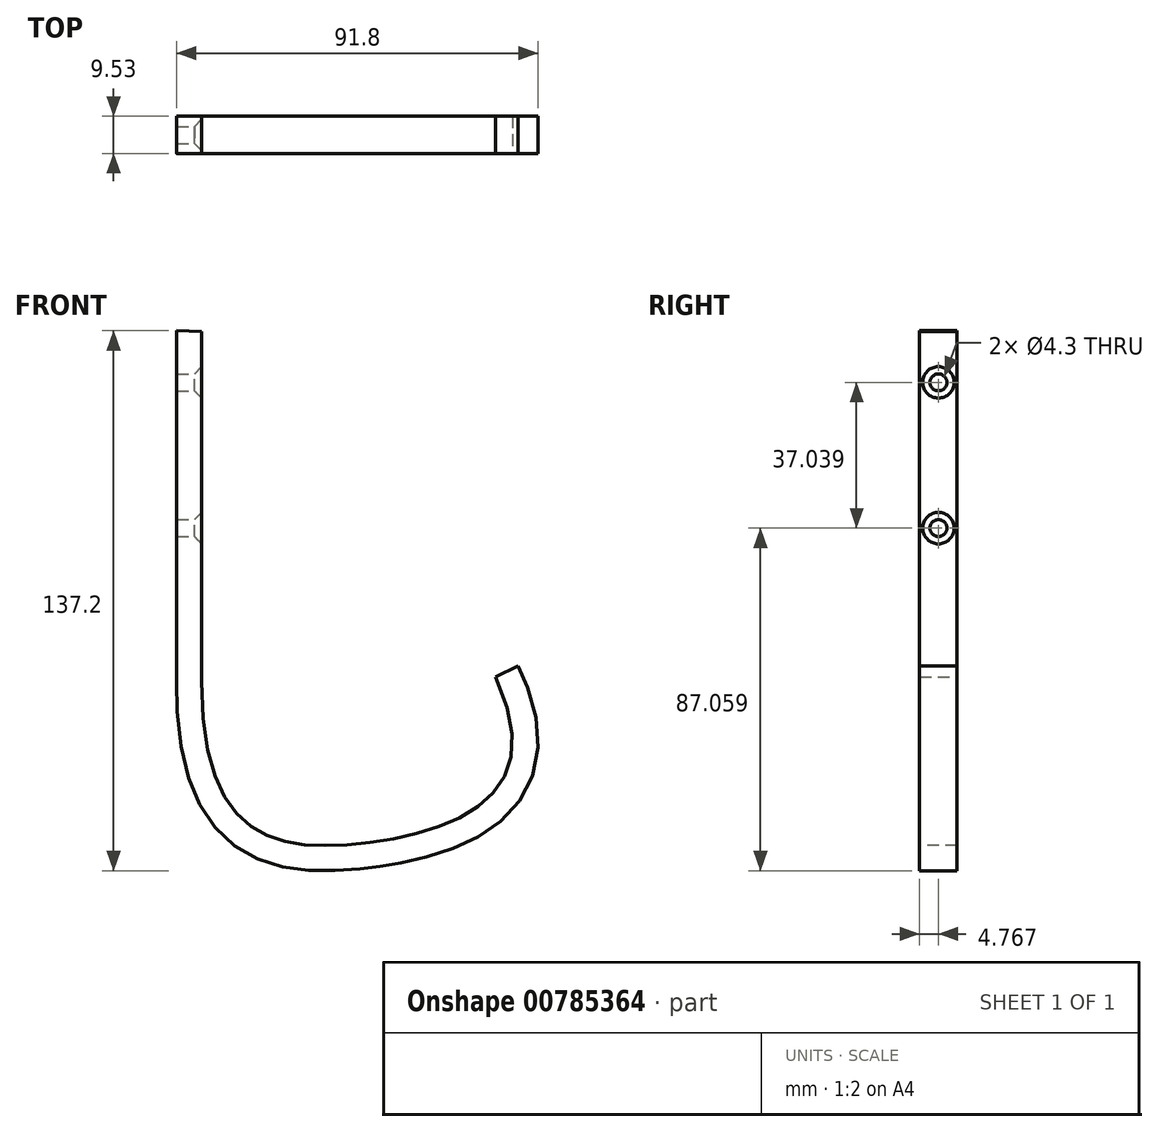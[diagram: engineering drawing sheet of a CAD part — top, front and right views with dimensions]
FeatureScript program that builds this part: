
annotation { "Feature Type Name" : "Feature", "Feature Type Description" : "" }
export const myFeature = defineFeature(function(context is Context, id is Id, definition is map)
    precondition{}
    {
        {
            var Q0;
            Q0=qCreatedBy(makeId("Front.planeOp"),FACE);
            var sketch = newSketch(context, id + "F0", { "sketchPlane" : qUnion([Q0])});
            skLineSegment(sketch, "E0", {"start": v(-38.57, 47.63) * mm, "end": v(-38.57, -41.27) * mm});
            skFitSpline(sketch, "E1", {"points": [v(-38.57, -41.27) * mm, v(2.43, -82.32) * mm, v(36.03, -40.1) * mm], "startDerivative": vector(0, -233.55) * mm, "endDerivative": vector(-90.62, 189.33) * mm});
            skFitSpline(sketch, "E2.0", {"points": [v(-44.92, -41.27) * mm, v(-44.92, -46.38) * mm, v(-44.5, -53.3) * mm, v(-43.08, -61.23) * mm, v(-41.58, -66.6) * mm, v(-39.63, -71.39) * mm, v(-37.22, -75.64) * mm, v(-34.35, -79.32) * mm, v(-31.05, -82.4) * mm, v(-27.41, -84.86) * mm, v(-23.53, -86.7) * mm, v(-19.49, -88) * mm, v(-15.34, -88.82) * mm, v(-11.12, -89.24) * mm, v(-6.84, -89.34) * mm, v(-2.51, -89.17) * mm, v(1.14, -88.85) * mm, v(4.08, -88.52) * mm, v(6.32, -88.23) * mm, v(8.58, -87.9) * mm, v(11.61, -87.38) * mm, v(15.43, -86.6) * mm, v(19.98, -85.42) * mm, v(24.44, -83.95) * mm, v(28.76, -82.14) * mm, v(32.88, -79.93) * mm, v(36.7, -77.24) * mm, v(40.15, -74.01) * mm, v(43.06, -70.17) * mm, v(45.24, -65.71) * mm, v(46.53, -60.73) * mm, v(46.84, -55.36) * mm, v(46.17, -49.7) * mm, v(44.54, -43.72) * mm, v(42.8, -39.52) * mm, v(41.76, -37.35) * mm]});
            skLineSegment(sketch, "E2.1", {"start": v(-44.92, 47.86) * mm, "end": v(-44.92, -41.27) * mm});
            skLineSegment(sketch, "E3", {"start": v(-44.92, 47.86) * mm, "end": v(-38.57, 47.63) * mm});
            skLineSegment(sketch, "E4", {"start": v(36.03, -40.1) * mm, "end": v(41.76, -37.35) * mm});
            skSolve(sketch);
        }
        {
            var Q0;
            Q0=makeQuery(id+"F0.imprint","IMPRINT",FACE,{"disambiguationData":[TD([[makeQuery(id+"F0.imprint","IMPRINT",EDGE,{"derivedFrom":sQuery(id+"F0.wireOp",EDGE,"E0")}),-1.0]])]});
            extrude(context, id + "F1", {"entities" : qUnion([Q0]), "depth" : 9.52 * mm, "offsetDistance" : 25.4 * mm});
        }
        {
            var Q0;
            Q0=makeQuery(id+"F1.opExtrude","SWEPT_FACE",FACE,{"disambiguationData":[OSD([sQuery(id+"F0.wireOp",EDGE,"E0")])]});
            var sketch = newSketch(context, id + "F2", { "sketchPlane" : qUnion([Q0])});
            skPoint(sketch, "E5", {"position": v(-4.76, 34.76) * mm});
            skPoint(sketch, "E6", {"position": v(-4.76, -2.28) * mm});
            skLineSegment(sketch, "E7", {"start": v(-4.76, 34.76) * mm, "end": v(0, 34.76) * mm});
            skLineSegment(sketch, "E8", {"start": v(0, 34.76) * mm, "end": v(-9.53, 34.76) * mm});
            skSolve(sketch);
        }
        {
            var Q0;
            Q0=sQuery(id+"F2.wireOp",VERTEX,"E5");
            var Q1;
            Q1=sQuery(id+"F2.wireOp",VERTEX,"E6");
            var Q2;
            Q2=makeQuery(id+"F1.opExtrude","SWEPT_BODY",BODY,{"disambiguationData":[OSD([sQuery(id+"F0.wireOp",EDGE,"E0"),sQuery(id+"F0.wireOp",EDGE,"E1"),sQuery(id+"F0.wireOp",EDGE,"E2.0"),sQuery(id+"F0.wireOp",EDGE,"E2.1"),sQuery(id+"F0.wireOp",EDGE,"E3"),sQuery(id+"F0.wireOp",EDGE,"E4")])]});
            hole(context, id + "F3", {"style" : HoleStyle.C_SINK, "endStyle" : HoleEndStyle.THROUGH, "holeDiameter" : 4.3 * mm, "cSinkDiameter" : 8 * mm, "cSinkAngle" : 90 * degree, "majorDiameter" : 6.35 * mm, "isTappedThrough" : true, "tappedDepth" : 12.7 * mm, "tapClearance" : 3, "locations" : qUnion([Q0, Q1]), "scope" : qUnion([Q2])});
        }
    });
